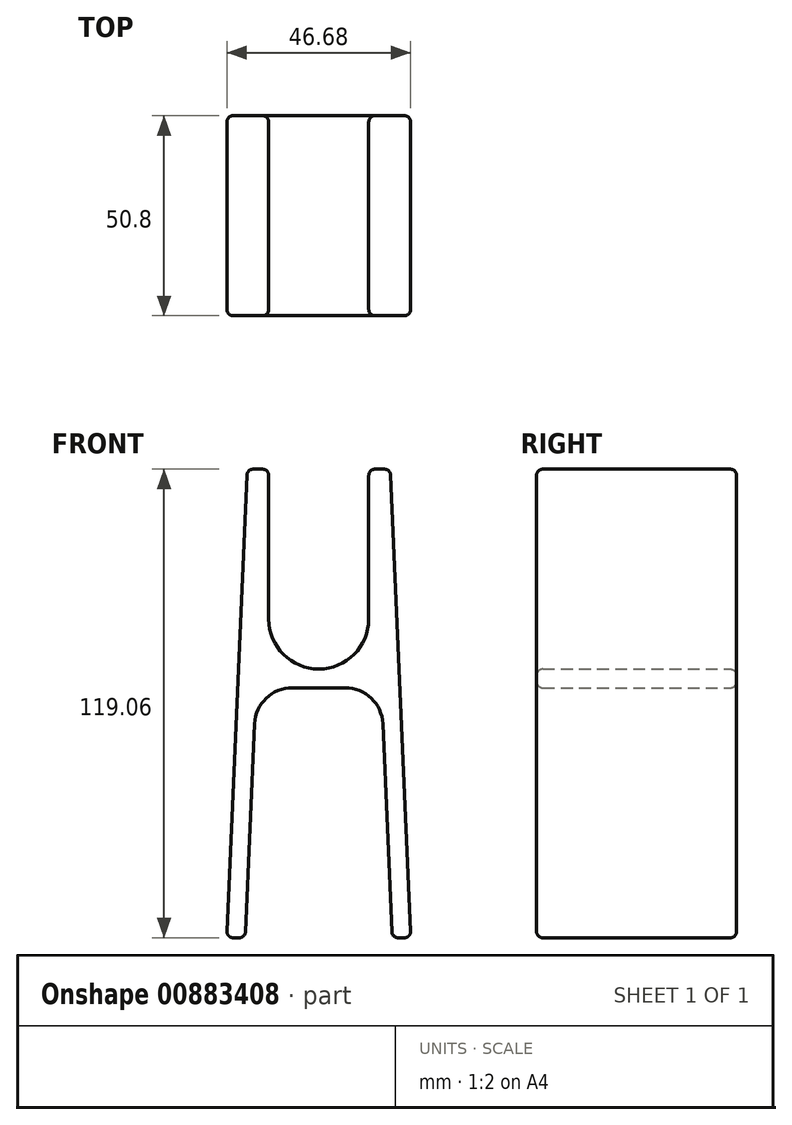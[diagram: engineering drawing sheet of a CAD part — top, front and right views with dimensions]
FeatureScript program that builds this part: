
annotation { "Feature Type Name" : "Feature", "Feature Type Description" : "" }
export const myFeature = defineFeature(function(context is Context, id is Id, definition is map)
    precondition{}
    {
        {
            var Q0;
            Q0=qCreatedBy(makeId("Front.planeOp"),FACE);
            var sketch = newSketch(context, id + "F0", { "sketchPlane" : qUnion([Q0])});
            skLineSegment(sketch, "E0", {"start": v(-23.4, -63.5) * mm, "end": v(-18.65, -63.5) * mm});
            skLineSegment(sketch, "E1", {"start": v(-18.65, -63.5) * mm, "end": v(-16.27, -9.1) * mm});
            skLineSegment(sketch, "E2", {"start": v(-6.76, 0) * mm, "end": v(0, 0) * mm});
            skLineSegment(sketch, "E3", {"start": v(0, 0) * mm, "end": v(0, 4.76) * mm});
            skLineSegment(sketch, "E4", {"start": v(0, 4.76) * mm, "end": v(0, 4.76) * mm});
            skLineSegment(sketch, "E5", {"start": v(-12.7, 17.46) * mm, "end": v(-12.7, 55.56) * mm});
            skLineSegment(sketch, "E6", {"start": v(-12.7, 55.56) * mm, "end": v(-18.21, 55.56) * mm});
            skLineSegment(sketch, "E7", {"start": v(-18.21, 55.56) * mm, "end": v(-23.4, -63.5) * mm});
            skLineSegment(sketch, "E8", {"start": v(0, 0) * mm, "end": v(0, -63.5) * mm, "construction": true});
            skLineSegment(sketch, "E9.MirrorCS", {"start": v(18.65, -63.5) * mm, "end": v(16.27, -9.1) * mm});
            skLineSegment(sketch, "E10.MirrorCS", {"start": v(23.4, -63.5) * mm, "end": v(18.65, -63.5) * mm});
            skLineSegment(sketch, "E11.MirrorCS", {"start": v(18.21, 55.56) * mm, "end": v(23.4, -63.5) * mm});
            skLineSegment(sketch, "E12.MirrorCS", {"start": v(12.7, 55.56) * mm, "end": v(18.21, 55.56) * mm});
            skLineSegment(sketch, "E13.MirrorCS", {"start": v(12.7, 17.46) * mm, "end": v(12.7, 55.56) * mm});
            skLineSegment(sketch, "E14.MirrorCS", {"start": v(6.76, 0) * mm, "end": v(0, 0) * mm});
            skPoint(sketch, "E15.visualSharp", {"position": v(-15.88, 0) * mm});
            skArc(sketch, "E15.filletArc", {"start": v(-6.76, 0) * mm, "mid": v(-13.34, -2.64) * mm, "end": v(-16.27, -9.1) * mm});
            skPoint(sketch, "E16.visualSharp", {"position": v(15.88, 0) * mm});
            skArc(sketch, "E16.filletArc", {"start": v(16.27, -9.1) * mm, "mid": v(13.34, -2.64) * mm, "end": v(6.76, 0) * mm});
            skPoint(sketch, "E17.visualSharp", {"position": v(12.7, 4.76) * mm});
            skArc(sketch, "E17.filletArc", {"start": v(0, 4.76) * mm, "mid": v(8.98, 8.48) * mm, "end": v(12.7, 17.46) * mm});
            skPoint(sketch, "E18.visualSharp", {"position": v(-12.7, 4.76) * mm});
            skArc(sketch, "E18.filletArc", {"start": v(-12.7, 17.46) * mm, "mid": v(-8.98, 8.48) * mm, "end": v(0, 4.76) * mm});
            skSolve(sketch);
        }
        {
            var Q0;
            Q0=makeQuery(id+"F0.imprint","IMPRINT",FACE,{"disambiguationData":[TD([[makeQuery(id+"F0.imprint","IMPRINT",EDGE,{"derivedFrom":sQuery(id+"F0.wireOp",EDGE,"E0")}),1.0]])]});
            var Q1;
            Q1=makeQuery(id+"F0.imprint","IMPRINT",FACE,{"disambiguationData":[TD([[makeQuery(id+"F0.imprint","IMPRINT",EDGE,{"derivedFrom":sQuery(id+"F0.wireOp",EDGE,"E9.MirrorCS")}),-1.0]])]});
            extrude(context, id + "F1", {"entities" : qUnion([Q0, Q1]), "depth" : 50.8 * mm, "offsetDistance" : 25.4 * mm});
        }
        {
            var Q0;
            Q0=makeQuery(id+"F1.opExtrude","CAP_FACE",FACE,{"disambiguationData":[OSD([sQuery(id+"F0.wireOp",EDGE,"E0"),sQuery(id+"F0.wireOp",EDGE,"E1"),sQuery(id+"F0.wireOp",EDGE,"E2"),sQuery(id+"F0.wireOp",EDGE,"E5"),sQuery(id+"F0.wireOp",EDGE,"E6"),sQuery(id+"F0.wireOp",EDGE,"E7"),sQuery(id+"F0.wireOp",EDGE,"E9.MirrorCS"),sQuery(id+"F0.wireOp",EDGE,"E10.MirrorCS"),sQuery(id+"F0.wireOp",EDGE,"E11.MirrorCS"),sQuery(id+"F0.wireOp",EDGE,"E12.MirrorCS"),sQuery(id+"F0.wireOp",EDGE,"E13.MirrorCS"),sQuery(id+"F0.wireOp",EDGE,"E14.MirrorCS"),sQuery(id+"F0.wireOp",EDGE,"E15.filletArc"),sQuery(id+"F0.wireOp",EDGE,"E16.filletArc"),sQuery(id+"F0.wireOp",EDGE,"E17.filletArc"),sQuery(id+"F0.wireOp",EDGE,"E18.filletArc")])],"isStart":false});
            var Q1;
            Q1=makeQuery(id+"F1.opExtrude","CAP_FACE",FACE,{"disambiguationData":[OSD([sQuery(id+"F0.wireOp",EDGE,"E0"),sQuery(id+"F0.wireOp",EDGE,"E1"),sQuery(id+"F0.wireOp",EDGE,"E2"),sQuery(id+"F0.wireOp",EDGE,"E5"),sQuery(id+"F0.wireOp",EDGE,"E6"),sQuery(id+"F0.wireOp",EDGE,"E7"),sQuery(id+"F0.wireOp",EDGE,"E9.MirrorCS"),sQuery(id+"F0.wireOp",EDGE,"E10.MirrorCS"),sQuery(id+"F0.wireOp",EDGE,"E11.MirrorCS"),sQuery(id+"F0.wireOp",EDGE,"E12.MirrorCS"),sQuery(id+"F0.wireOp",EDGE,"E13.MirrorCS"),sQuery(id+"F0.wireOp",EDGE,"E14.MirrorCS"),sQuery(id+"F0.wireOp",EDGE,"E15.filletArc"),sQuery(id+"F0.wireOp",EDGE,"E16.filletArc"),sQuery(id+"F0.wireOp",EDGE,"E17.filletArc"),sQuery(id+"F0.wireOp",EDGE,"E18.filletArc")])],"isStart":true});
            fillet(context, id + "F2", {"entities" : qUnion([Q0, Q1]), "radius" : 1.59 * mm, "tangentPropagation" : true, "allowEdgeOverflow" : false});
        }
        {
            var Q0;
            Q0=makeQuery(id+"F1.opExtrude","SWEPT_FACE",FACE,{"disambiguationData":[OSD([sQuery(id+"F0.wireOp",EDGE,"E7")])]});
            var Q1;
            Q1=makeQuery(id+"F1.opExtrude","SWEPT_FACE",FACE,{"disambiguationData":[OSD([sQuery(id+"F0.wireOp",EDGE,"E11.MirrorCS")])]});
            fillet(context, id + "F3", {"entities" : qUnion([Q0, Q1]), "radius" : 1.59 * mm, "tangentPropagation" : true, "allowEdgeOverflow" : false});
        }
        {
            var Q0;
            Q0=makeQuery(id+"F1.opExtrude","SWEPT_EDGE",EDGE,{"disambiguationData":[OSD([sQuery(id+"F0.wireOp",EDGE,"E5"),sQuery(id+"F0.wireOp",EDGE,"E6")])]});
            var Q1;
            Q1=makeQuery(id+"F1.opExtrude","SWEPT_EDGE",EDGE,{"disambiguationData":[OSD([sQuery(id+"F0.wireOp",EDGE,"E12.MirrorCS"),sQuery(id+"F0.wireOp",EDGE,"E13.MirrorCS")])]});
            var Q2;
            Q2=makeQuery(id+"F1.opExtrude","SWEPT_EDGE",EDGE,{"disambiguationData":[OSD([sQuery(id+"F0.wireOp",EDGE,"E0"),sQuery(id+"F0.wireOp",EDGE,"E1")])]});
            var Q3;
            Q3=makeQuery(id+"F1.opExtrude","SWEPT_EDGE",EDGE,{"disambiguationData":[OSD([sQuery(id+"F0.wireOp",EDGE,"E9.MirrorCS"),sQuery(id+"F0.wireOp",EDGE,"E10.MirrorCS")])]});
            fillet(context, id + "F4", {"entities" : qUnion([Q0, Q1, Q2, Q3]), "radius" : 1.59 * mm, "tangentPropagation" : true, "allowEdgeOverflow" : false});
        }
    });
